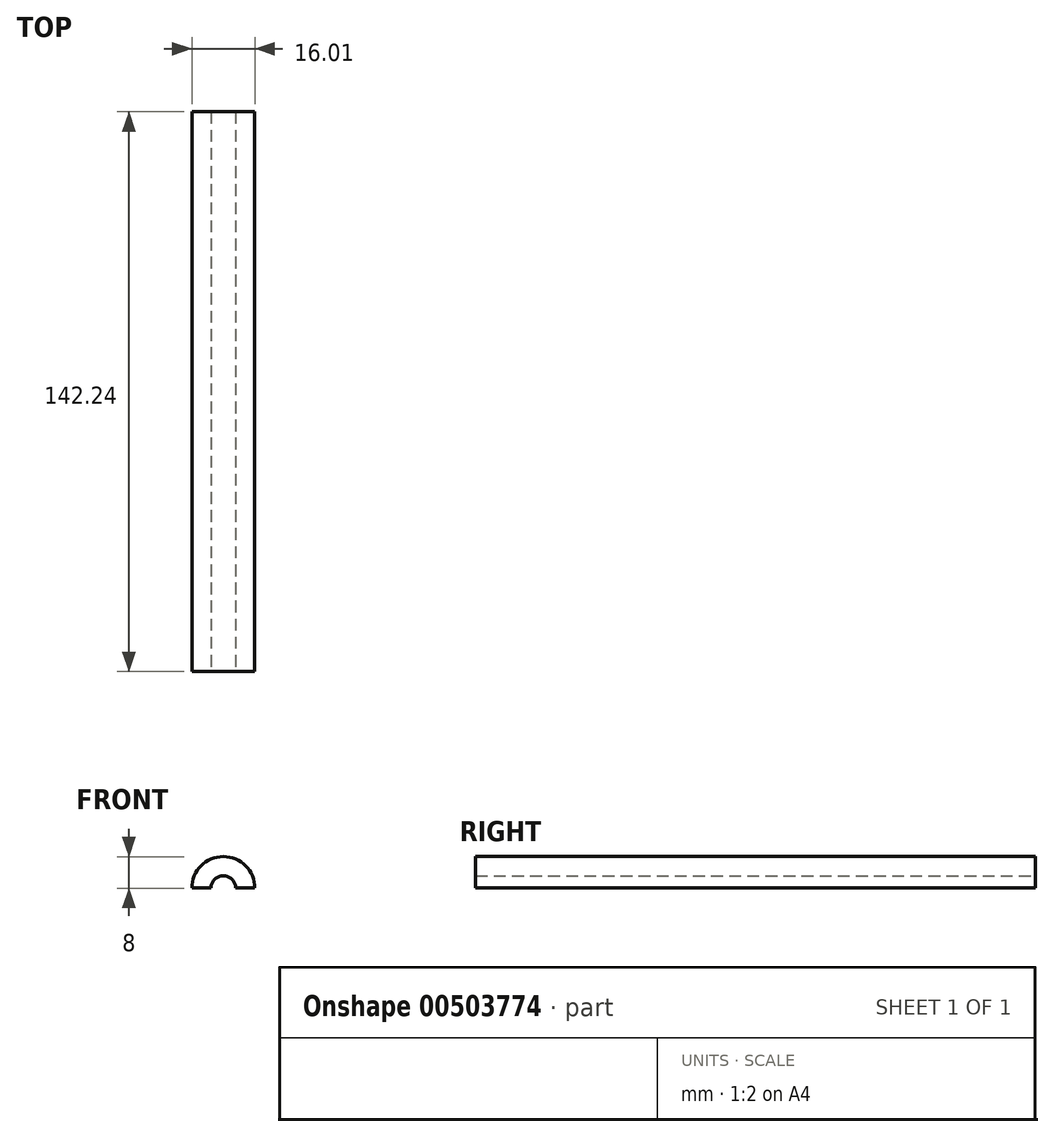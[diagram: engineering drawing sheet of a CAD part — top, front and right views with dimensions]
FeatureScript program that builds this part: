
annotation { "Feature Type Name" : "Feature", "Feature Type Description" : "" }
export const myFeature = defineFeature(function(context is Context, id is Id, definition is map)
    precondition{}
    {
        {
            var Q0;
            Q0=qCreatedBy(makeId("Front.planeOp"),FACE);
            var sketch = newSketch(context, id + "F0", { "sketchPlane" : qUnion([Q0])});
            skCircle(sketch, "E0", {"center": v(-40.3, 23.76) * mm, "radius": 8 * mm});
            skCircle(sketch, "E1", {"center": v(-40.3, 23.76) * mm, "radius": 3.15 * mm});
            skSolve(sketch);
        }
        {
            var Q0;
            Q0 = qSketchRegion(id + "F0", true);
            extrude(context, id + "F1", {"entities" : qUnion([Q0]), "depth" : 142.24 * mm});
        }
        {
            var Q0;
            Q0=makeQuery(id+"F1.opExtrude","CAP_FACE",FACE,{"disambiguationData":[OSD([sQuery(id+"F0.wireOp",EDGE,"E0"),sQuery(id+"F0.wireOp",EDGE,"E1")])],"isStart":false});
            var sketch = newSketch(context, id + "F2", { "sketchPlane" : qUnion([Q0])});
            skLineSegment(sketch, "E2", {"start": v(-40.3, 23.76) * mm, "end": v(-30.55, 23.76) * mm});
            skLineSegment(sketch, "E3", {"start": v(-30.55, 23.76) * mm, "end": v(-30.55, 15.95) * mm});
            skLineSegment(sketch, "E4", {"start": v(-30.55, 15.95) * mm, "end": v(-43.7, 13.9) * mm});
            skLineSegment(sketch, "E5", {"start": v(-43.7, 13.9) * mm, "end": v(-53.44, 19) * mm});
            skLineSegment(sketch, "E6", {"start": v(-53.44, 19) * mm, "end": v(-52.81, 23.76) * mm});
            skLineSegment(sketch, "E7", {"start": v(-52.81, 23.76) * mm, "end": v(-40.3, 23.76) * mm});
            skSolve(sketch);
        }
        {
            var Q0;
            {var subQ0=sQuery(id+"F2.wireOp",EDGE,"E3");Q0=makeQuery(id+"F2.imprint","IMPRINT",FACE,{"disambiguationData":[TD([[makeQuery(id+"F2.imprint","IMPRINT",EDGE,{"derivedFrom":subQ0}),-1.0]])]});}
            var Q1;
            {var subQ0=sQuery(id+"F2.wireOp",EDGE,"E2");var subQ1=makeQuery(id+"F1.opExtrude","CAP_EDGE",EDGE,{"disambiguationData":[OSD([sQuery(id+"F0.wireOp",EDGE,"E0")])],"isStart":false});var subQ2=makeQuery(id+"F2.imprint","INTERSECT",VERTEX,{"derivedFrom":[subQ1,subQ0]});Q1=makeQuery(id+"F2.imprint","IMPRINT",FACE,{"disambiguationData":[TD([[makeQuery(id+"F2.imprint","IMPRINT",EDGE,{"disambiguationData":[TD([[subQ2,1.0]])],"derivedFrom":subQ0}),-1.0]])]});}
            extrude(context, id + "F3", {"entities" : qUnion([Q0, Q1]), "operationType" : NewBodyOperationType.REMOVE, "oppositeDirection" : true, "depth" : 269.5 * mm});
        }
    });
